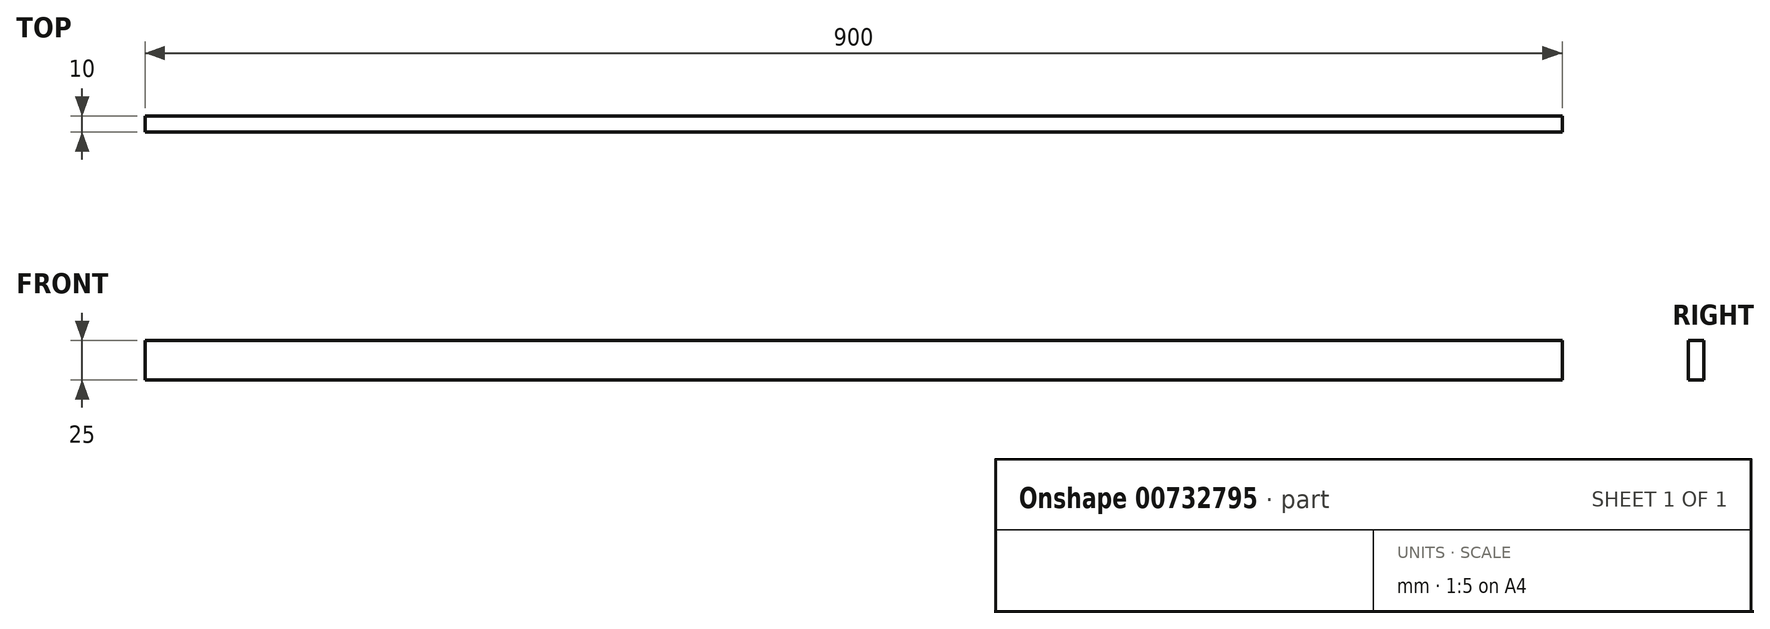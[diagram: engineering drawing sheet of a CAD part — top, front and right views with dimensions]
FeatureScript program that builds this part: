
annotation { "Feature Type Name" : "Feature", "Feature Type Description" : "" }
export const myFeature = defineFeature(function(context is Context, id is Id, definition is map)
    precondition{}
    {
        {
            var Q0;
            Q0=qCreatedBy(makeId("Front.planeOp"),FACE);
            var sketch = newSketch(context, id + "F0", { "sketchPlane" : qUnion([Q0])});
            skLineSegment(sketch, "E0.bottom", {"start": v(-443.03, -125.68) * mm, "end": v(456.97, -125.68) * mm});
            skLineSegment(sketch, "E0.top", {"start": v(-443.03, -150.68) * mm, "end": v(456.97, -150.68) * mm});
            skLineSegment(sketch, "E0.left", {"start": v(-443.03, -125.68) * mm, "end": v(-443.03, -150.68) * mm});
            skLineSegment(sketch, "E0.right", {"start": v(456.97, -125.68) * mm, "end": v(456.97, -150.68) * mm});
            skSolve(sketch);
        }
        {
            var Q0;
            Q0 = qSketchRegion(id + "F0", true);
            extrude(context, id + "F1", {"entities" : qUnion([Q0]), "depth" : 10 * mm, "offsetDistance" : 25 * mm});
        }
    });
